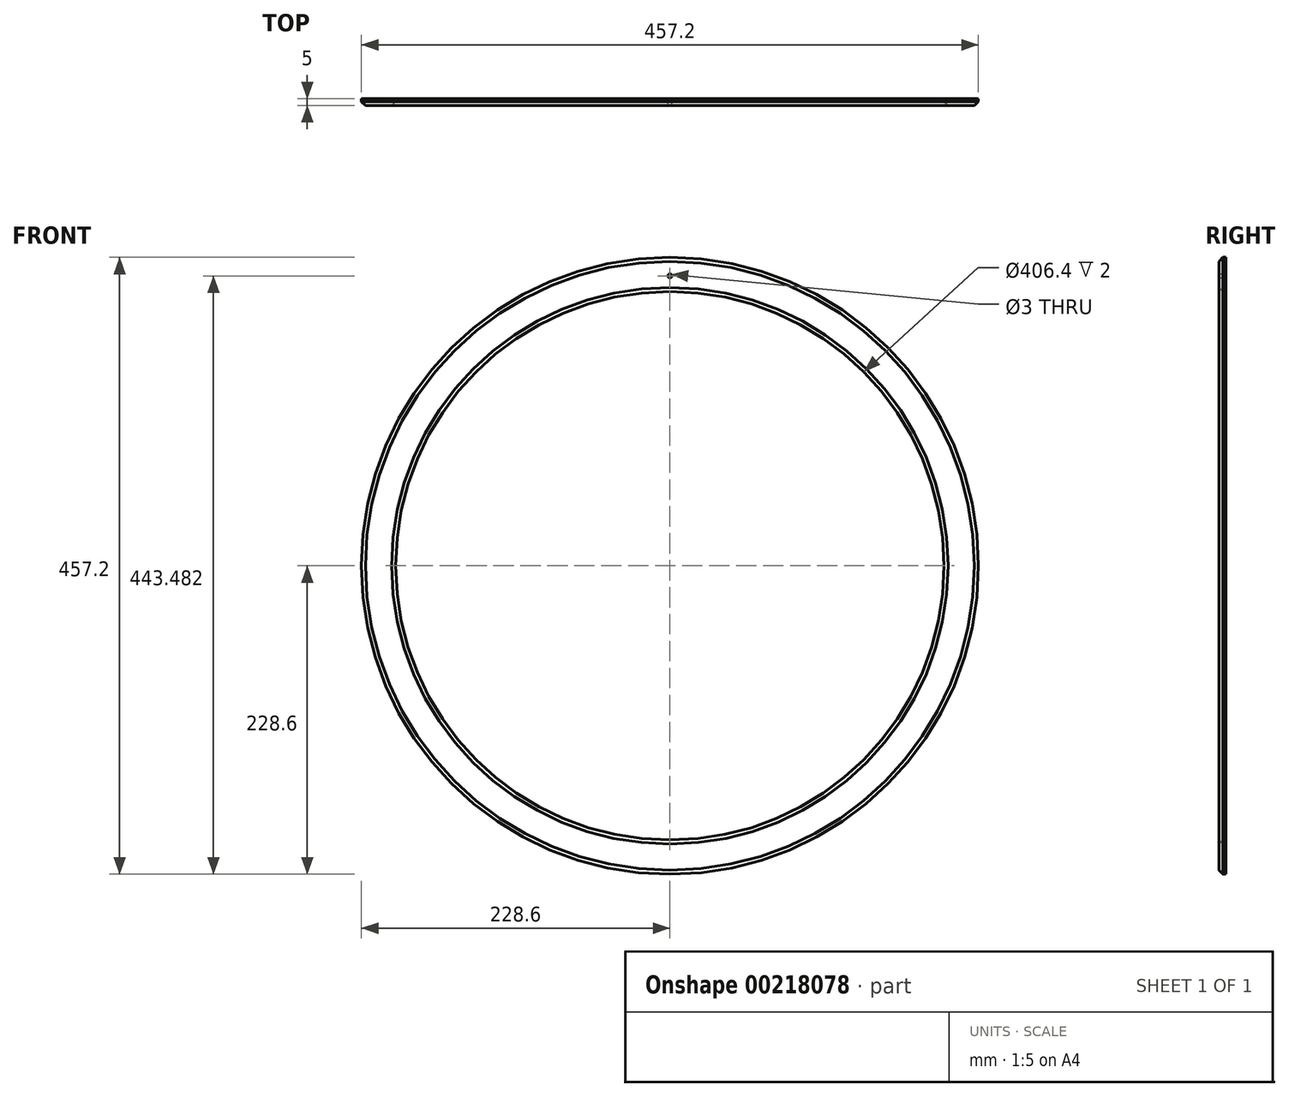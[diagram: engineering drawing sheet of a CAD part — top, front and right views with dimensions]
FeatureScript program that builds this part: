
annotation { "Feature Type Name" : "Feature", "Feature Type Description" : "" }
export const myFeature = defineFeature(function(context is Context, id is Id, definition is map)
    precondition{}
    {
        {
            var Q0;
            Q0=qCreatedBy(makeId("Front.planeOp"),FACE);
            var sketch = newSketch(context, id + "F0", { "sketchPlane" : qUnion([Q0])});
            skCircle(sketch, "E0", {"center": v(0, 0) * mm, "radius": 228.6 * mm});
            skCircle(sketch, "E1", {"center": v(0, 0) * mm, "radius": 203.2 * mm});
            skLineSegment(sketch, "E2", {"start": v(0, 238.57) * mm, "end": v(0, -228.6) * mm, "construction": true});
            skCircle(sketch, "E3", {"center": v(0, 214.88) * mm, "radius": 1.5 * mm});
            skCircle(sketch, "E4", {"center": v(0, -215.12) * mm, "radius": 1.5 * mm});
            skSolve(sketch);
        }
        {
            var Q0;
            Q0=makeQuery(id+"F0.imprint","IMPRINT",FACE,{"disambiguationData":[TD([[makeQuery(id+"F0.imprint","IMPRINT",EDGE,{"derivedFrom":sQuery(id+"F0.wireOp",EDGE,"E0")}),1.0]])]});
            var Q1;
            Q1=makeQuery(id+"F0.imprint","IMPRINT",FACE,{"disambiguationData":[TD([[makeQuery(id+"F0.imprint","IMPRINT",EDGE,{"derivedFrom":sQuery(id+"F0.wireOp",EDGE,"E4")}),1.0]])]});
            extrude(context, id + "F1", {"entities" : qUnion([Q0, Q1]), "depth" : 5 * mm});
        }
        {
            var Q0;
            Q0=makeQuery(id+"F1.opExtrude","CAP_EDGE",EDGE,{"disambiguationData":[OSD([sQuery(id+"F0.wireOp",EDGE,"E0")])],"isStart":false});
            var Q1;
            Q1=makeQuery(id+"F1.opExtrude","CAP_EDGE",EDGE,{"disambiguationData":[OSD([sQuery(id+"F0.wireOp",EDGE,"E1")])],"isStart":false});
            chamfer(context, id + "F2", {"entities" : qUnion([Q0, Q1]), "width" : 3 * mm, "tangentPropagation" : true});
        }
    });
